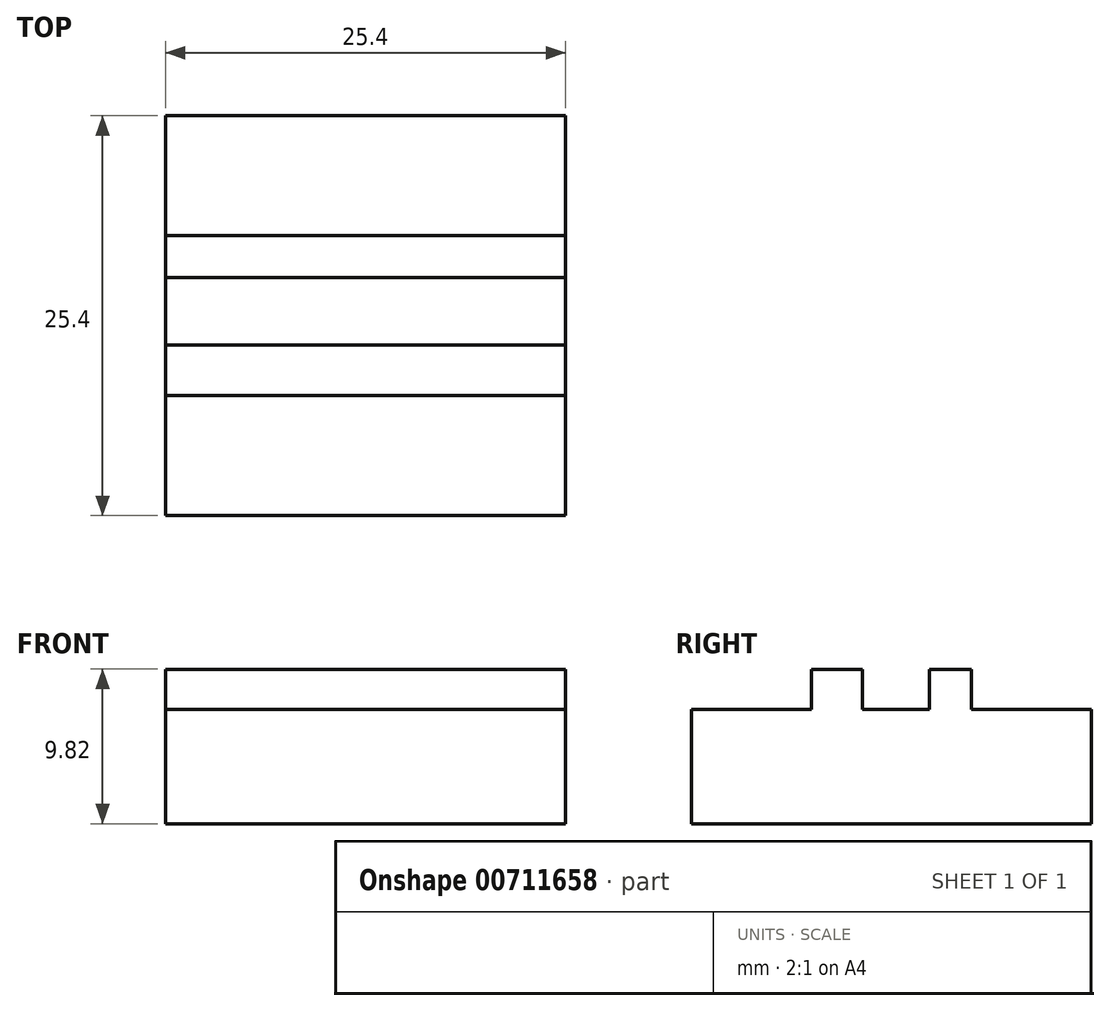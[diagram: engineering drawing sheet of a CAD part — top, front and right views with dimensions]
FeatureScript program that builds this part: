
annotation { "Feature Type Name" : "Feature", "Feature Type Description" : "" }
export const myFeature = defineFeature(function(context is Context, id is Id, definition is map)
    precondition{}
    {
        {
            var Q0;
            Q0=qCreatedBy(makeId("Right.planeOp"),FACE);
            var sketch = newSketch(context, id + "F0", { "sketchPlane" : qUnion([Q0])});
            skLineSegment(sketch, "E0", {"start": v(0, 0) * mm, "end": v(0, 7.28) * mm});
            skLineSegment(sketch, "E1", {"start": v(0, 7.28) * mm, "end": v(-7.62, 7.28) * mm});
            skLineSegment(sketch, "E2", {"start": v(-7.62, 7.28) * mm, "end": v(-7.62, 9.82) * mm});
            skLineSegment(sketch, "E3", {"start": v(-7.62, 9.82) * mm, "end": v(-10.27, 9.82) * mm});
            skLineSegment(sketch, "E4", {"start": v(-10.27, 9.82) * mm, "end": v(-10.27, 7.28) * mm});
            skLineSegment(sketch, "E5", {"start": v(-10.27, 7.28) * mm, "end": v(-14.56, 7.28) * mm});
            skLineSegment(sketch, "E6", {"start": v(-14.56, 7.28) * mm, "end": v(-14.56, 9.82) * mm});
            skLineSegment(sketch, "E7", {"start": v(-14.56, 9.82) * mm, "end": v(-17.78, 9.82) * mm});
            skLineSegment(sketch, "E8", {"start": v(-17.78, 9.82) * mm, "end": v(-17.78, 7.28) * mm});
            skLineSegment(sketch, "E9", {"start": v(-17.78, 7.28) * mm, "end": v(-25.4, 7.28) * mm});
            skLineSegment(sketch, "E10", {"start": v(-25.4, 7.28) * mm, "end": v(-25.4, 0) * mm});
            skLineSegment(sketch, "E11", {"start": v(0, 0) * mm, "end": v(-25.4, 0) * mm});
            skSolve(sketch);
        }
        {
            var Q0;
            Q0=makeQuery(id+"F0.imprint","IMPRINT",FACE,{"disambiguationData":[TD([[makeQuery(id+"F0.imprint","IMPRINT",EDGE,{"derivedFrom":sQuery(id+"F0.wireOp",EDGE,"E0")}),1.0]])]});
            extrude(context, id + "F1", {"entities" : qUnion([Q0]), "depth" : 25.4 * mm, "offsetDistance" : 25.4 * mm});
        }
    });
